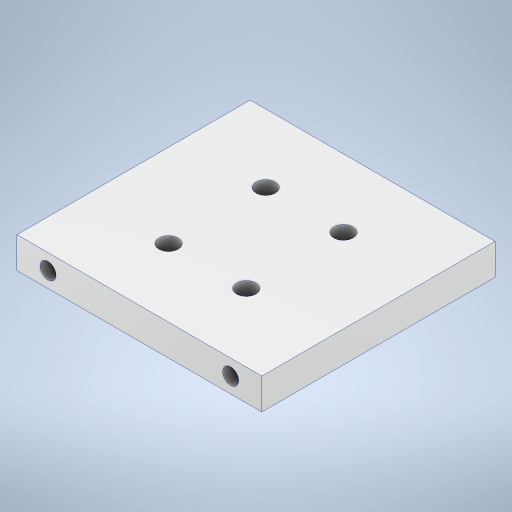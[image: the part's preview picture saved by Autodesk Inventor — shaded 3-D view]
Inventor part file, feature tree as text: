
AUTODESK INVENTOR PART (.ipt)
format: ipt  version: 2023 (Build 270158000, 158)  size: 275,968 bytes
history: native  units: mm
features: sketch x4, hole x3, other x3, extrude x1
ambient origin geometry x8: Origin, YZ Plane, XZ Plane, XY Plane, X Axis, Y Axis, Z Axis, Center Point
bodies: Body1 (feature_tree)
feature tree (11):
  extrude  "Extrusion2"  Depth=63.0mm
  hole  "Hole3"  [1 undecoded]
  hole  "Hole4"  [1 undecoded]
  hole  "Hole5"  [1 undecoded]
  sketch  "Sketch5"  dims[d43=53.25mm d68=63.0mm]
  sketch  "Sketch6"  dims[d69=60.0mm d70=8.0mm d71=0.0mm]
  sketch  "Sketch7"  dims[d72=20.0mm d74=25.0mm d75=20.0mm d77=20.0mm d80=63.0mm]
  sketch  "Sketch8"  dims[d81=60.0mm d82=21.5mm d83=17.5mm d84=5.0mm d85=6.0mm d86=4.0mm d87=2.0mm d88=90.0deg d89=5.0mm d90=20.594885mm d91=8.0mm d92=8.0mm d93=4.134mm d94=10.0mm d95=4.0mm d96=2.0mm d97=90.0deg d98=14.2mm d99=20.594885mm d100=4.134mm d101=10.0mm d102=4.0mm d103=2.0mm d104=90.0deg d105=14.2mm d106=20.594885mm d0=0.0mm d1=10.0mm d2=73.0mm]
  other  "Definição1"
  other  "Annotations"
  other  "Linear Dimension 1"
note: 3 required parameter values undecoded (feature->parameter linkage not recoverable at this tier; creation-order binding heuristic only, values carry confidence <= 0.55)
